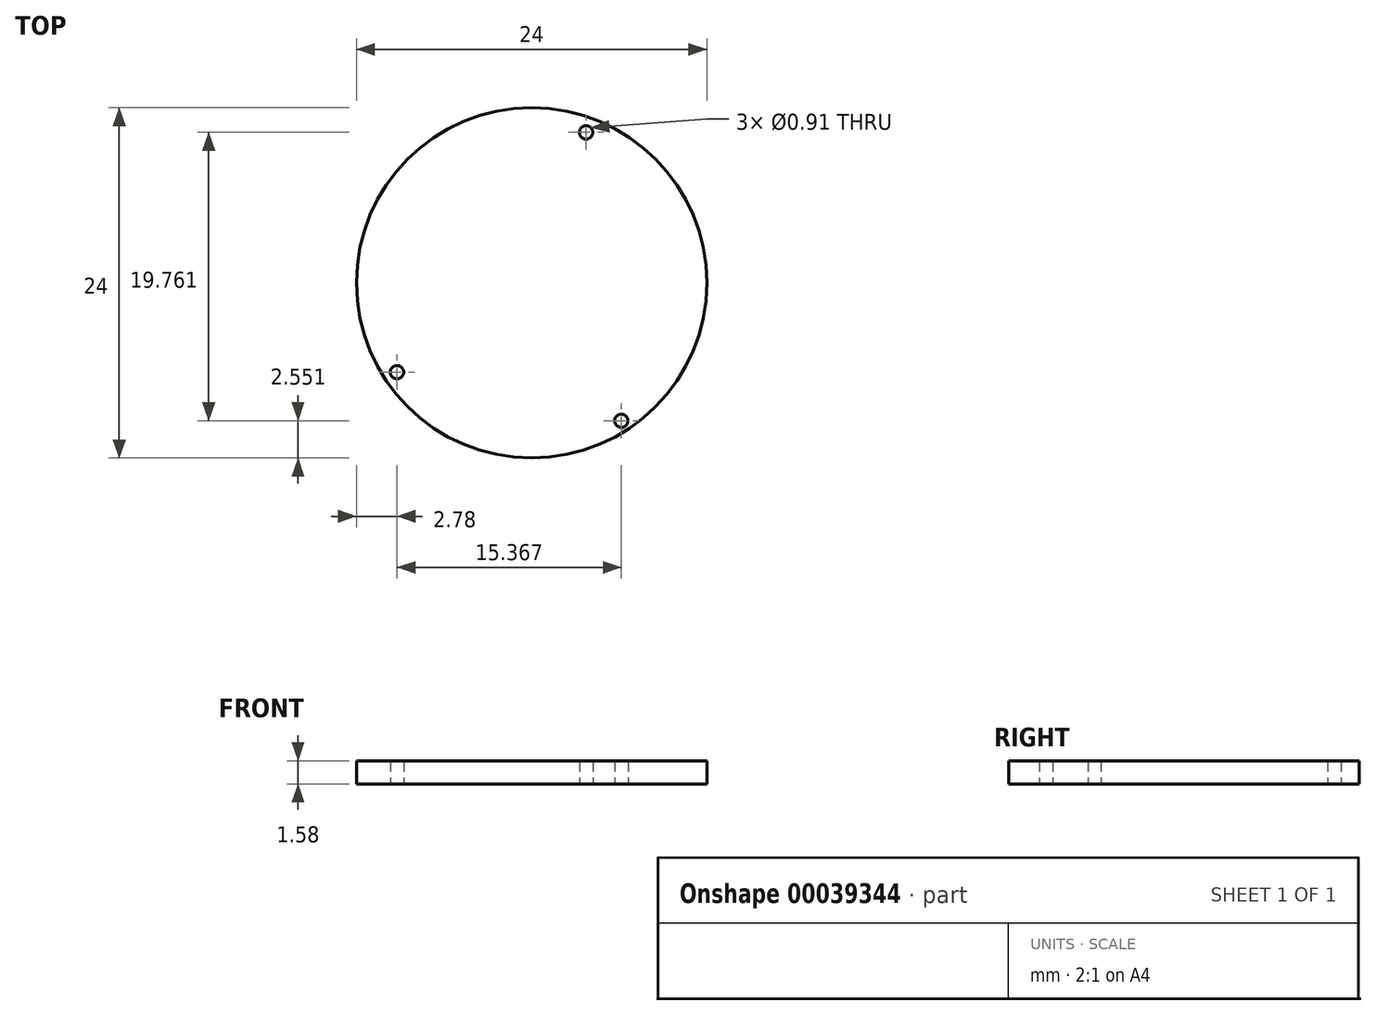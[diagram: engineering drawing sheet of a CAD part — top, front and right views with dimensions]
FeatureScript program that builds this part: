
annotation { "Feature Type Name" : "Feature", "Feature Type Description" : "" }
export const myFeature = defineFeature(function(context is Context, id is Id, definition is map)
    precondition{}
    {
        {
            var Q0;
            Q0=qCreatedBy(makeId("Top.planeOp"),FACE);
            var sketch = newSketch(context, id + "F0", { "sketchPlane" : qUnion([Q0])});
            skCircle(sketch, "E0", {"center": v(0, 0) * mm, "radius": 12 * mm});
            skLineSegment(sketch, "E1", {"start": v(0, 0) * mm, "end": v(6.15, -9.45) * mm, "construction": true});
            skLineSegment(sketch, "E2", {"start": v(0, 0) * mm, "end": v(-9.22, -6.12) * mm, "construction": true});
            skLineSegment(sketch, "E3", {"start": v(0, 0) * mm, "end": v(3.73, 10.31) * mm, "construction": true});
            skLineSegment(sketch, "E4", {"start": v(0, 0) * mm, "end": v(19.05, 0) * mm, "construction": true});
            skCircle(sketch, "E5", {"center": v(-9.22, -6.12) * mm, "radius": 0.46 * mm});
            skCircle(sketch, "E6", {"center": v(3.73, 10.31) * mm, "radius": 0.46 * mm});
            skCircle(sketch, "E7", {"center": v(6.15, -9.45) * mm, "radius": 0.46 * mm});
            skSolve(sketch);
        }
        {
            var Q0;
            Q0=makeQuery(id+"F0.imprint","IMPRINT",FACE,{"disambiguationData":[TD([[makeQuery(id+"F0.imprint","IMPRINT",EDGE,{"derivedFrom":sQuery(id+"F0.wireOp",EDGE,"E0")}),1.0]])]});
            extrude(context, id + "F1", {"entities" : qUnion([Q0]), "depth" : 1.58 * mm});
        }
    });
